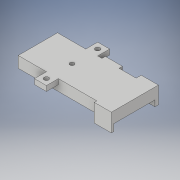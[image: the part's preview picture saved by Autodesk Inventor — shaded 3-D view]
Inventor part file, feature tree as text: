
AUTODESK INVENTOR PART (.ipt)
format: ipt  version: 2018 (Build 220112000, 112)  size: 267,264 bytes
history: native  units: in
note: dims shown in document units (in); Inventor stores cm internally (conversion verified against a paired STEP export)
features: extrude x15, sketch x15, projected_geometry x1
ambient origin geometry x8: Origin, YZ Plane, XZ Plane, XY Plane, X Axis, Y Axis, Z Axis, Center Point
bodies: Solid1 (feature_tree)
feature tree (31):
  extrude  "Extrusion1"  Depth=0.3937in
  extrude  "Extrusion2"  Depth=0.0394in TaperAngle=0.0deg
  extrude  "Extrusion3"  Depth=0.0394in TaperAngle=0.0deg
  extrude  "Extrusion4"  Depth=0.6693in TaperAngle=0.0deg
  extrude  "Extrusion5"  TaperAngle=0.0deg  [1 undecoded]
  extrude  "Extrusion10"  Depth=2.2047in
  extrude  "Extrusion11"  TaperAngle=0.0deg  [1 undecoded]
  extrude  "Extrusion12"  Depth=0.7874in
  extrude  "Extrusion13"  Depth=0.7874in
  extrude  "Extrusion14"  TaperAngle=0.0deg  [1 undecoded]
  extrude  "Extrusion18"  Depth=0.2756in
  extrude  "Extrusion19"  Depth=0.2756in
  extrude  "Extrusion20"  Depth=0.1083in
  extrude  "Extrusion21"  TaperAngle=0.0deg  [1 undecoded]
  extrude  "Extrusion22"  Depth=0.3937in
  sketch  "Sketch1"  dims[d0=0.3937in d1=0.3937in]
  sketch  "Sketch2"  dims[d2=0.1181in d3=0.0394in d4=0.0in]
  sketch  "Sketch3"  dims[d5=0.0591in d6=0.0394in d7=0.0in]
  sketch  "Sketch4"  dims[d8=0.0591in d9=0.6693in d10=0.0in]
  sketch  "Sketch5"  dims[d11=0.0591in d12=0.0in d13=0.0in]
  sketch  "Sketch11"  dims[d14=0.0591in d15=2.2047in]
  sketch  "Sketch12"  dims[d16=0.9055in d17=0.0in d42=0.0in]
  sketch  "Sketch13"  dims[d45=0.0984in d46=0.7874in]
  sketch  "Sketch14"  dims[d47=0.1969in d48=0.0in d49=0.7874in]
  sketch  "Sketch15"  dims[d50=0.0in d51=0.0in]
  sketch  "Sketch19"  dims[d52=0.2756in d53=0.2756in]
  sketch  "Sketch20"  dims[d54=0.2756in d55=0.2756in]
  sketch  "Sketch21"  dims[d56=0.1083in d57=0.1083in]
  sketch  "Sketch22"  dims[d58=0.1181in d59=0.0in d60=0.0in]
  sketch  "Sketch23"  dims[d61=0.1181in d62=0.3937in d63=0.3937in d64=0.0in d65=0.0394in d66=0.0in d67=0.1575in d68=0.0in d69=0.7874in d70=0.0in d80=1.1811in d81=0.0in d82=0.7874in d83=0.3937in d84=0.0787in d85=0.5709in d86=0.0in d87=0.0394in d88=0.3937in d89=0.0in d90=0.0984in d91=0.3937in d92=0.0in d93=0.2559in d94=0.0in]
  projected_geometry  "Projected Loop1"
note: 4 required parameter values undecoded (feature->parameter linkage not recoverable at this tier; creation-order binding heuristic only, values carry confidence <= 0.55)
